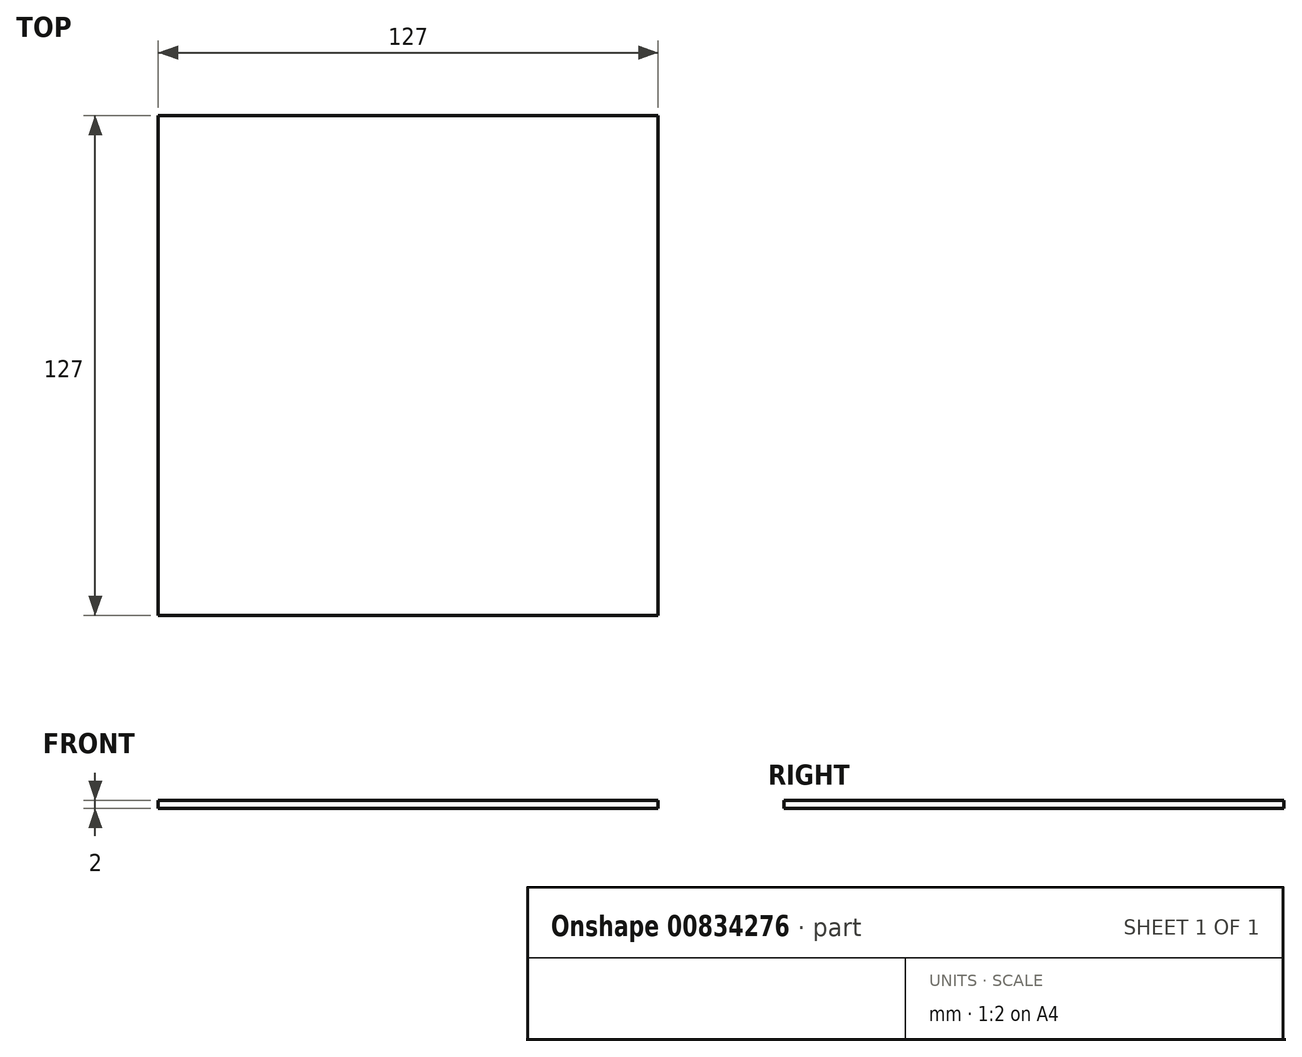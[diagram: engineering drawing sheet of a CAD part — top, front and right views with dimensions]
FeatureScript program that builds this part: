
annotation { "Feature Type Name" : "Feature", "Feature Type Description" : "" }
export const myFeature = defineFeature(function(context is Context, id is Id, definition is map)
    precondition{}
    {
        {
            var Q0;
            Q0=qCreatedBy(makeId("Top.planeOp"),FACE);
            var sketch = newSketch(context, id + "F0", { "sketchPlane" : qUnion([Q0])});
            skLineSegment(sketch, "E0.bottom", {"start": v(-60.98, 63.7) * mm, "end": v(66.02, 63.7) * mm});
            skLineSegment(sketch, "E0.top", {"start": v(-60.98, -63.3) * mm, "end": v(66.02, -63.3) * mm});
            skLineSegment(sketch, "E0.left", {"start": v(-60.98, 63.7) * mm, "end": v(-60.98, -63.3) * mm});
            skLineSegment(sketch, "E0.right", {"start": v(66.02, 63.7) * mm, "end": v(66.02, -63.3) * mm});
            skSolve(sketch);
        }
        {
            var Q0;
            Q0 = qSketchRegion(id + "F0", true);
            extrude(context, id + "F1", {"entities" : qUnion([Q0]), "depth" : 2 * mm, "offsetDistance" : 25 * mm});
        }
    });
